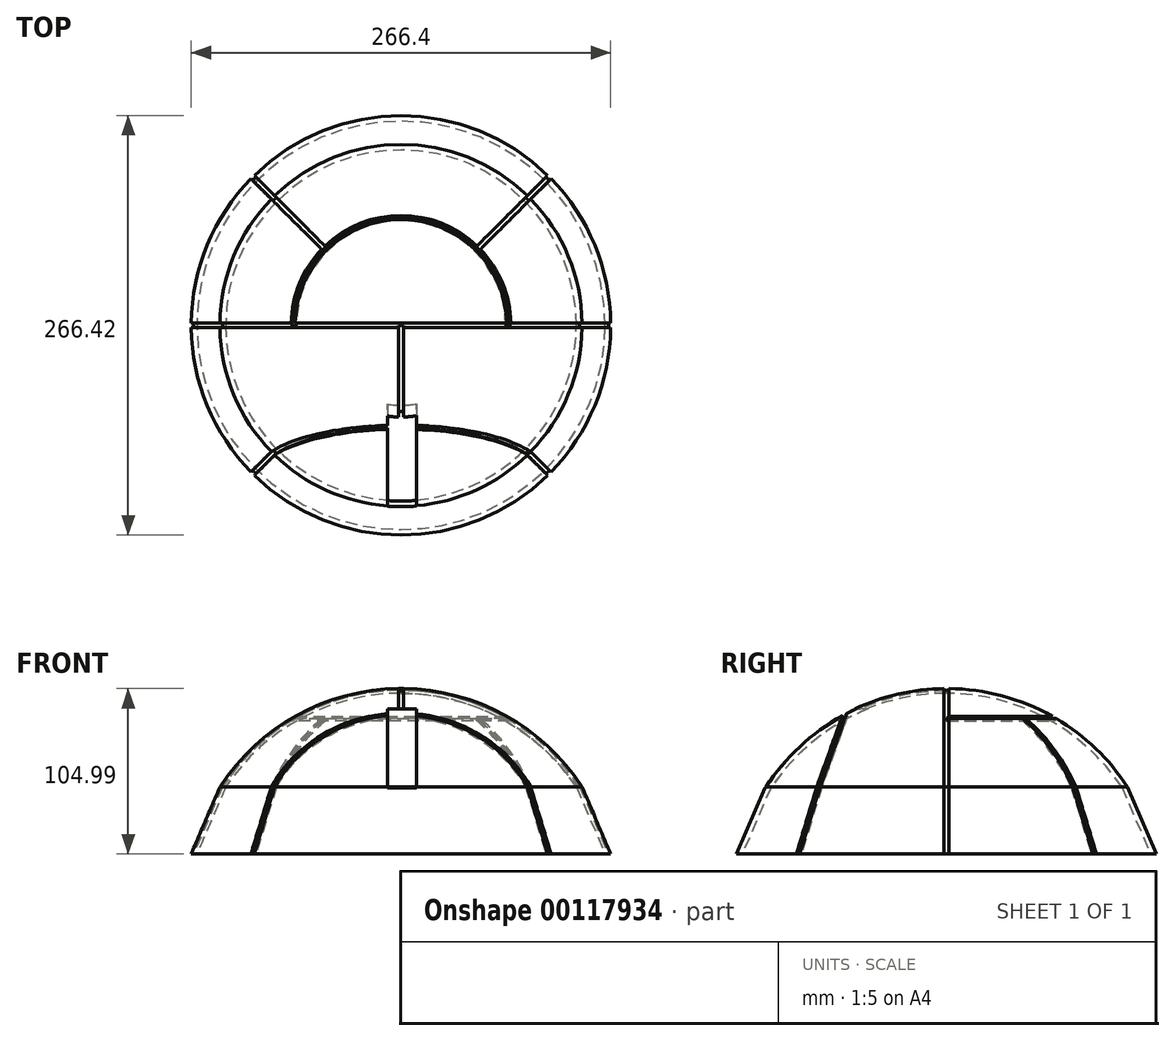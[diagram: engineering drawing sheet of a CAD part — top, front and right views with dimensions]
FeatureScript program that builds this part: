
annotation { "Feature Type Name" : "Feature", "Feature Type Description" : "" }
export const myFeature = defineFeature(function(context is Context, id is Id, definition is map)
    precondition{}
    {
        {
            var Q0;
            Q0=qCreatedBy(makeId("Front.planeOp"),FACE);
            var sketch = newSketch(context, id + "F0", { "sketchPlane" : qUnion([Q0])});
            skArc(sketch, "E0", {"start": v(114.97, 74.5) * mm, "mid": v(0, 137) * mm, "end": v(-114.97, 74.5) * mm});
            skLineSegment(sketch, "E1", {"start": v(-137, 0) * mm, "end": v(137, 0) * mm});
            skLineSegment(sketch, "E2", {"start": v(-133.21, 32) * mm, "end": v(133.21, 32) * mm});
            skLineSegment(sketch, "E3", {"start": v(-114.97, 74.5) * mm, "end": v(114.97, 74.5) * mm});
            skLineSegment(sketch, "E4", {"start": v(-114.97, 74.5) * mm, "end": v(-133.21, 32) * mm});
            skLineSegment(sketch, "E5", {"start": v(114.97, 74.5) * mm, "end": v(133.21, 32) * mm});
            skLineSegment(sketch, "E6", {"start": v(0, 137) * mm, "end": v(-99.44, 137) * mm, "construction": true});
            skLineSegment(sketch, "E7", {"start": v(0, 0) * mm, "end": v(0, 137) * mm});
            skArc(sketch, "E8", {"start": v(130.12, 32) * mm, "mid": v(0, 134) * mm, "end": v(-130.12, 32) * mm});
            skLineSegment(sketch, "E9", {"start": v(-111.38, 74.5) * mm, "end": v(-129.62, 32) * mm});
            skLineSegment(sketch, "E10", {"start": v(111.38, 74.5) * mm, "end": v(130.12, 32) * mm});
            skSolve(sketch);
        }
        {
            var Q0;
            {var subQ0=sQuery(id+"F0.wireOp",EDGE,"E4");Q0=makeQuery(id+"F0.imprint","IMPRINT",FACE,{"disambiguationData":[TD([[makeQuery(id+"F0.imprint","IMPRINT",EDGE,{"derivedFrom":subQ0}),1.0]])]});}
            var Q1;
            {var subQ0=sQuery(id+"F0.wireOp",EDGE,"E9");var subQ5=sQuery(id+"F0.wireOp",EDGE,"E2");var subQ7=makeQuery(id+"F0.imprint","INTERSECT",VERTEX,{"derivedFrom":[subQ5,subQ0]});Q1=makeQuery(id+"F0.imprint","IMPRINT",FACE,{"disambiguationData":[TD([[makeQuery(id+"F0.imprint","IMPRINT",EDGE,{"disambiguationData":[TD([[subQ7,1.0]])],"derivedFrom":subQ5}),1.0]])]});}
            var Q2;
            {var subQ0=sQuery(id+"F0.wireOp",EDGE,"y0KMc1JP-Vqzv-Jfck-pHGM-2HrRGkrfssAq");Q2=makeQuery(id+"F0.imprint","IMPRINT",FACE,{"disambiguationData":[TD([[makeQuery(id+"F0.imprint","IMPRINT",EDGE,{"derivedFrom":subQ0}),-1.0]])]});}
            var Q3;
            {var subQ1=sQuery(id+"F0.wireOp",EDGE,"E0");var subQ3=sQuery(id+"F0.wireOp",EDGE,"E7");var subQ4=makeQuery(id+"F0.imprint","INTERSECT",VERTEX,{"derivedFrom":[subQ1,subQ3]});Q3=makeQuery(id+"F0.imprint","IMPRINT",FACE,{"disambiguationData":[TD([[makeQuery(id+"F0.imprint","IMPRINT",EDGE,{"disambiguationData":[TD([[subQ4,1.0]])],"derivedFrom":subQ3}),1.0]])]});}
            var Q4;
            Q4=sQuery(id+"F0.wireOp",EDGE,"E7");
            revolve(context, id + "F1", {"entities" : qUnion([Q0, Q1, Q2, Q3]), "axis" : qUnion([Q4]), "revolveType" : RevolveType.FULL});
        }
        {
            var Q0;
            Q0=qCreatedBy(makeId("Top.planeOp"),FACE);
            cPlane(context, id + "F2", {"entities" : qUnion([Q0]), "cplaneType" : CPlaneType.OFFSET, "offset" : 74.5 * mm, "width" : 150 * mm, "height" : 150 * mm});
        }
        {
            var Q0;
            Q0=qCreatedBy(id+"F2.planeOp",FACE);
            var sketch = newSketch(context, id + "F3", { "sketchPlane" : qUnion([Q0])});
            skLineSegment(sketch, "E11", {"start": v(0, 0) * mm, "end": v(-58.68, 0) * mm, "construction": true});
            skLineSegment(sketch, "E12.bottom", {"start": v(-113.47, 1.5) * mm, "end": v(-116.47, 1.5) * mm});
            skLineSegment(sketch, "E12.top", {"start": v(-113.47, -1.5) * mm, "end": v(-116.47, -1.5) * mm});
            skLineSegment(sketch, "E12.left", {"start": v(-113.47, 1.5) * mm, "end": v(-113.47, -1.5) * mm});
            skLineSegment(sketch, "E12.right", {"start": v(-116.47, 1.5) * mm, "end": v(-116.47, -1.5) * mm});
            skPoint(sketch, "E12.middle", {"position": v(-114.97, 0) * mm});
            skLineSegment(sketch, "E13.1.0", {"start": v(-81.3, -79.18) * mm, "end": v(-83.42, -81.3) * mm});
            skLineSegment(sketch, "E13.1.1", {"start": v(-81.3, -79.18) * mm, "end": v(-79.18, -81.3) * mm});
            skLineSegment(sketch, "E13.1.2", {"start": v(-79.18, -81.3) * mm, "end": v(-81.3, -83.42) * mm});
            skLineSegment(sketch, "E13.1.3", {"start": v(-83.42, -81.3) * mm, "end": v(-81.3, -83.42) * mm});
            skLineSegment(sketch, "E13.2.0", {"start": v(-1.5, -113.47) * mm, "end": v(-1.5, -116.47) * mm});
            skLineSegment(sketch, "E13.2.1", {"start": v(-1.5, -113.47) * mm, "end": v(1.5, -113.47) * mm});
            skLineSegment(sketch, "E13.2.2", {"start": v(1.5, -113.47) * mm, "end": v(1.5, -116.47) * mm});
            skLineSegment(sketch, "E13.2.3", {"start": v(-1.5, -116.47) * mm, "end": v(1.5, -116.47) * mm});
            skLineSegment(sketch, "E13.3.0", {"start": v(79.18, -81.3) * mm, "end": v(81.3, -83.42) * mm});
            skLineSegment(sketch, "E13.3.1", {"start": v(79.18, -81.3) * mm, "end": v(81.3, -79.18) * mm});
            skLineSegment(sketch, "E13.3.2", {"start": v(81.3, -79.18) * mm, "end": v(83.42, -81.3) * mm});
            skLineSegment(sketch, "E13.3.3", {"start": v(81.3, -83.42) * mm, "end": v(83.42, -81.3) * mm});
            skLineSegment(sketch, "E13.4.0", {"start": v(113.47, -1.5) * mm, "end": v(116.47, -1.5) * mm});
            skLineSegment(sketch, "E13.4.1", {"start": v(113.47, -1.5) * mm, "end": v(113.47, 1.5) * mm});
            skLineSegment(sketch, "E13.4.2", {"start": v(113.47, 1.5) * mm, "end": v(116.47, 1.5) * mm});
            skLineSegment(sketch, "E13.4.3", {"start": v(116.47, -1.5) * mm, "end": v(116.47, 1.5) * mm});
            skLineSegment(sketch, "E13.5.0", {"start": v(81.3, 79.18) * mm, "end": v(83.42, 81.3) * mm});
            skLineSegment(sketch, "E13.5.1", {"start": v(81.3, 79.18) * mm, "end": v(79.18, 81.3) * mm});
            skLineSegment(sketch, "E13.5.2", {"start": v(79.18, 81.3) * mm, "end": v(81.3, 83.42) * mm});
            skLineSegment(sketch, "E13.5.3", {"start": v(83.42, 81.3) * mm, "end": v(81.3, 83.42) * mm});
            skLineSegment(sketch, "E13.6.0", {"start": v(1.5, 113.47) * mm, "end": v(1.5, 116.47) * mm});
            skLineSegment(sketch, "E13.6.1", {"start": v(1.5, 113.47) * mm, "end": v(-1.5, 113.47) * mm});
            skLineSegment(sketch, "E13.6.2", {"start": v(-1.5, 113.47) * mm, "end": v(-1.5, 116.47) * mm});
            skLineSegment(sketch, "E13.6.3", {"start": v(1.5, 116.47) * mm, "end": v(-1.5, 116.47) * mm});
            skLineSegment(sketch, "E13.7.0", {"start": v(-79.18, 81.3) * mm, "end": v(-81.3, 83.42) * mm});
            skLineSegment(sketch, "E13.7.1", {"start": v(-79.18, 81.3) * mm, "end": v(-81.3, 79.18) * mm});
            skLineSegment(sketch, "E13.7.2", {"start": v(-81.3, 79.18) * mm, "end": v(-83.42, 81.3) * mm});
            skLineSegment(sketch, "E13.7.3", {"start": v(-81.3, 83.42) * mm, "end": v(-83.42, 81.3) * mm});
            skPoint(sketch, "E13.center", {"position": v(0, 0) * mm});
            skLineSegment(sketch, "E14", {"start": v(81.3, -81.3) * mm, "end": v(-81.3, 81.3) * mm, "construction": true});
            skLineSegment(sketch, "E15", {"start": v(81.3, 81.3) * mm, "end": v(-81.3, -81.3) * mm, "construction": true});
            skLineSegment(sketch, "E16", {"start": v(-81.3, -81.3) * mm, "end": v(81.3, -81.3) * mm, "construction": true});
            skSolve(sketch);
        }
        {
            var Q0;
            Q0=makeQuery(id+"F3.imprint","IMPRINT",FACE,{"disambiguationData":[TD([[makeQuery(id+"F3.imprint","IMPRINT",EDGE,{"derivedFrom":sQuery(id+"F3.wireOp",EDGE,"E12.bottom")}),1.0]])]});
            var Q1;
            Q1=sQuery(id+"F0.wireOp",EDGE,"E4");
            sweep(context, id + "F4", {"operationType" : NewBodyOperationType.REMOVE, "profiles" : qUnion([Q0]), "path" : qUnion([Q1])});
        }
        {
            var Q0;
            Q0=makeQuery(id+"F3.imprint","IMPRINT",FACE,{"disambiguationData":[TD([[makeQuery(id+"F3.imprint","IMPRINT",EDGE,{"derivedFrom":sQuery(id+"F3.wireOp",EDGE,"E12.bottom")}),1.0]])]});
            var Q1;
            Q1=sQuery(id+"F0.wireOp",EDGE,"E0");
            sweep(context, id + "F5", {"operationType" : NewBodyOperationType.REMOVE, "profiles" : qUnion([Q0]), "path" : qUnion([Q1])});
        }
        {
            var Q0;
            Q0=makeQuery(id+"F3.imprint","IMPRINT",FACE,{"disambiguationData":[TD([[makeQuery(id+"F3.imprint","IMPRINT",EDGE,{"derivedFrom":sQuery(id+"F3.wireOp",EDGE,"E13.4.0")}),1.0]])]});
            var Q1;
            Q1=sQuery(id+"F0.wireOp",EDGE,"E5");
            sweep(context, id + "F6", {"operationType" : NewBodyOperationType.REMOVE, "profiles" : qUnion([Q0]), "path" : qUnion([Q1])});
        }
        {
            var Q0;
            Q0=qCreatedBy(makeId("Right.planeOp"),FACE);
            var sketch = newSketch(context, id + "F7", { "sketchPlane" : qUnion([Q0])});
            skArc(sketch, "E17", {"start": v(0, 137) * mm, "mid": v(-33.14, 132.93) * mm, "end": v(-64.32, 120.96) * mm});
            skLineSegment(sketch, "E18", {"start": v(0, 0) * mm, "end": v(-64.32, 120.96) * mm, "construction": true});
            skLineSegment(sketch, "E19", {"start": v(0, 137) * mm, "end": v(0, 0) * mm, "construction": true});
            skSolve(sketch);
        }
        {
            var Q0;
            Q0=qCreatedBy(makeId("Front.planeOp"),FACE);
            var sketch = newSketch(context, id + "F8", { "sketchPlane" : qUnion([Q0])});
            skLineSegment(sketch, "E20.bottom", {"start": v(1.5, 138.5) * mm, "end": v(-1.5, 138.5) * mm});
            skLineSegment(sketch, "E20.top", {"start": v(1.5, 135.5) * mm, "end": v(-1.5, 135.5) * mm});
            skLineSegment(sketch, "E20.left", {"start": v(1.5, 138.5) * mm, "end": v(1.5, 135.5) * mm});
            skLineSegment(sketch, "E20.right", {"start": v(-1.5, 138.5) * mm, "end": v(-1.5, 135.5) * mm});
            skPoint(sketch, "E20.middle", {"position": v(0, 137) * mm});
            skSolve(sketch);
        }
        {
            var Q0;
            Q0=makeQuery(id+"F8.imprint","IMPRINT",FACE,{"disambiguationData":[TD([[makeQuery(id+"F8.imprint","IMPRINT",EDGE,{"derivedFrom":sQuery(id+"F8.wireOp",EDGE,"E20.bottom")}),1.0]])]});
            var Q1;
            Q1=sQuery(id+"F7.wireOp",EDGE,"E17");
            sweep(context, id + "F9", {"operationType" : NewBodyOperationType.REMOVE, "profiles" : qUnion([Q0]), "path" : qUnion([Q1])});
        }
        {
            var Q0;
            Q0=qCreatedBy(makeId("Front.planeOp"),FACE);
            var sketch = newSketch(context, id + "F10", { "sketchPlane" : qUnion([Q0])});
            skCircle(sketch, "E21", {"center": v(0, 0) * mm, "radius": 137 * mm, "construction": true});
            skLineSegment(sketch, "E22", {"start": v(0, 0) * mm, "end": v(68.5, 118.65) * mm, "construction": true});
            skLineSegment(sketch, "E23", {"start": v(68.5, 118.65) * mm, "end": v(-68.5, 118.65) * mm});
            skLineSegment(sketch, "E24", {"start": v(-68.5, 118.65) * mm, "end": v(0, 0) * mm, "construction": true});
            skCircle(sketch, "E25", {"center": v(68.5, 118.65) * mm, "radius": 1.5 * mm});
            skLineSegment(sketch, "E26", {"start": v(67.75, 117.35) * mm, "end": v(69.05, 116.6) * mm});
            skLineSegment(sketch, "E27", {"start": v(69.05, 116.6) * mm, "end": v(70.55, 119.2) * mm});
            skLineSegment(sketch, "E28", {"start": v(67.75, 117.35) * mm, "end": v(66.45, 118.1) * mm});
            skLineSegment(sketch, "E29", {"start": v(70.55, 119.2) * mm, "end": v(67.95, 120.7) * mm});
            skLineSegment(sketch, "E30", {"start": v(67.95, 120.7) * mm, "end": v(66.45, 118.1) * mm});
            skSolve(sketch);
        }
        {
            var Q0;
            Q0=sQuery(id+"F10.wireOp",EDGE,"E23");
            cPlane(context, id + "F11", {"entities" : qUnion([Q0]), "cplaneType" : CPlaneType.LINE_ANGLE, "offset" : 25 * mm, "angle" : 90 * degree, "width" : 150 * mm, "height" : 150 * mm});
        }
        {
            var Q0;
            Q0=qCreatedBy(id+"F11.planeOp",FACE);
            var sketch = newSketch(context, id + "F12", { "sketchPlane" : qUnion([Q0])});
            skArc(sketch, "E31", {"start": v(68.5, 0) * mm, "mid": v(0, 68.5) * mm, "end": v(-68.5, 0) * mm});
            skLineSegment(sketch, "E32", {"start": v(-68.5, 0) * mm, "end": v(68.5, 0) * mm});
            skSolve(sketch);
        }
        {
            var Q0;
            {var subQ0=sQuery(id+"F10.wireOp",EDGE,"E25");var subQ3=makeQuery(id+"F10.imprint","INTERSECT",VERTEX,{"derivedFrom":[subQ0,sQuery(id+"F10.wireOp",EDGE,"E30")]});Q0=makeQuery(id+"F10.imprint","IMPRINT",FACE,{"disambiguationData":[TD([[makeQuery(id+"F10.imprint","IMPRINT",EDGE,{"disambiguationData":[TD([[subQ3,1.0]])],"derivedFrom":subQ0}),1.0]])]});}
            var Q1;
            {var subQ5=sQuery(id+"F10.wireOp",EDGE,"E28");Q1=makeQuery(id+"F10.imprint","IMPRINT",FACE,{"disambiguationData":[TD([[makeQuery(id+"F10.imprint","IMPRINT",EDGE,{"derivedFrom":subQ5}),-1.0]])]});}
            var Q2;
            {var subQ0=sQuery(id+"F10.wireOp",EDGE,"E30");var subQ1=sQuery(id+"F10.wireOp",EDGE,"E23");var subQ2=makeQuery(id+"F10.imprint","INTERSECT",VERTEX,{"derivedFrom":[subQ1,subQ0]});Q2=makeQuery(id+"F10.imprint","IMPRINT",FACE,{"disambiguationData":[TD([[makeQuery(id+"F10.imprint","IMPRINT",EDGE,{"disambiguationData":[TD([[subQ2,1.0]])],"derivedFrom":subQ1}),-1.0]])]});}
            var Q3;
            {var subQ0=sQuery(id+"F10.wireOp",EDGE,"E30");var subQ1=sQuery(id+"F10.wireOp",EDGE,"E25");var subQ2=makeQuery(id+"F10.imprint","INTERSECT",VERTEX,{"derivedFrom":[subQ1,subQ0]});Q3=makeQuery(id+"F10.imprint","IMPRINT",FACE,{"disambiguationData":[TD([[makeQuery(id+"F10.imprint","IMPRINT",EDGE,{"disambiguationData":[TD([[subQ2,1.0]])],"derivedFrom":subQ1}),-1.0]])]});}
            var Q4;
            {var subQ0=sQuery(id+"F10.wireOp",EDGE,"E29");var subQ1=sQuery(id+"F10.wireOp",EDGE,"E25");var subQ2=makeQuery(id+"F10.imprint","INTERSECT",VERTEX,{"derivedFrom":[subQ1,subQ0]});Q4=makeQuery(id+"F10.imprint","IMPRINT",FACE,{"disambiguationData":[TD([[makeQuery(id+"F10.imprint","IMPRINT",EDGE,{"disambiguationData":[TD([[subQ2,1.0]])],"derivedFrom":subQ1}),-1.0]])]});}
            var Q5;
            {var subQ0=sQuery(id+"F10.wireOp",EDGE,"E26");Q5=makeQuery(id+"F10.imprint","IMPRINT",FACE,{"disambiguationData":[TD([[makeQuery(id+"F10.imprint","IMPRINT",EDGE,{"derivedFrom":subQ0}),1.0]])]});}
            var Q6;
            Q6=sQuery(id+"F12.wireOp",EDGE,"E31");
            sweep(context, id + "F13", {"operationType" : NewBodyOperationType.REMOVE, "profiles" : qUnion([Q0, Q1, Q2, Q3, Q4, Q5]), "path" : qUnion([Q6])});
        }
        {
            var Q0;
            Q0=sQuery(id+"F3.wireOp",EDGE,"E15");
            cPlane(context, id + "F14", {"entities" : qUnion([Q0]), "cplaneType" : CPlaneType.LINE_ANGLE, "offset" : 25 * mm, "angle" : 90 * degree, "width" : 150 * mm, "height" : 150 * mm});
        }
        {
            var Q0;
            Q0=qCreatedBy(id+"F14.planeOp",FACE);
            var sketch = newSketch(context, id + "F15", { "sketchPlane" : qUnion([Q0])});
            skLineSegment(sketch, "E33", {"start": v(202.35, 74.5) * mm, "end": v(-236.58, 74.5) * mm, "construction": true});
            skLineSegment(sketch, "E34", {"start": v(177.5, 32) * mm, "end": v(-236.58, 32) * mm, "construction": true});
            skLineSegment(sketch, "E35", {"start": v(114.93, 74.5) * mm, "end": v(133.21, 32) * mm});
            skLineSegment(sketch, "E36", {"start": v(69.47, 117.89) * mm, "end": v(69.47, 32) * mm});
            skLineSegment(sketch, "E37", {"start": v(69.47, 32) * mm, "end": v(133.21, 32) * mm});
            skArc(sketch, "E38.trimOffspring", {"start": v(115.04, 74.26) * mm, "mid": v(94.8, 98.73) * mm, "end": v(69.47, 117.89) * mm});
            skSolve(sketch);
        }
        {
            var Q0;
            Q0=makeQuery(id+"F3.imprint","IMPRINT",FACE,{"disambiguationData":[TD([[makeQuery(id+"F3.imprint","IMPRINT",EDGE,{"derivedFrom":sQuery(id+"F3.wireOp",EDGE,"E13.5.0")}),1.0]])]});
            var Q1;
            Q1=sQuery(id+"F15.wireOp",EDGE,"E35");
            sweep(context, id + "F16", {"operationType" : NewBodyOperationType.REMOVE, "profiles" : qUnion([Q0]), "path" : qUnion([Q1])});
        }
        {
            var Q0;
            Q0=makeQuery(id+"F3.imprint","IMPRINT",FACE,{"disambiguationData":[TD([[makeQuery(id+"F3.imprint","IMPRINT",EDGE,{"derivedFrom":sQuery(id+"F3.wireOp",EDGE,"E13.5.0")}),1.0]])]});
            var Q1;
            Q1=sQuery(id+"F15.wireOp",EDGE,"E38.trimOffspring");
            sweep(context, id + "F17", {"operationType" : NewBodyOperationType.REMOVE, "profiles" : qUnion([Q0]), "path" : qUnion([Q1])});
        }
        {
            var Q0;
            Q0=sQuery(id+"F3.wireOp",EDGE,"E14");
            cPlane(context, id + "F18", {"entities" : qUnion([Q0]), "cplaneType" : CPlaneType.LINE_ANGLE, "offset" : 25 * mm, "angle" : 90 * degree, "width" : 150 * mm, "height" : 150 * mm});
        }
        {
            var Q0;
            Q0=qCreatedBy(id+"F18.planeOp",FACE);
            var sketch = newSketch(context, id + "F19", { "sketchPlane" : qUnion([Q0])});
            skArc(sketch, "E39", {"start": v(-114.97, 74.5) * mm, "mid": v(-125.9, 54.03) * mm, "end": v(-133.21, 32) * mm});
            skLineSegment(sketch, "E40", {"start": v(-154.96, 32) * mm, "end": v(196.04, 32) * mm, "construction": true});
            skLineSegment(sketch, "E41", {"start": v(-136.76, 74.5) * mm, "end": v(202.22, 74.5) * mm, "construction": true});
            skLineSegment(sketch, "E42", {"start": v(114.97, 74.5) * mm, "end": v(133.21, 32) * mm});
            skLineSegment(sketch, "E43", {"start": v(68.48, 118.66) * mm, "end": v(68.48, 32) * mm});
            skLineSegment(sketch, "E44", {"start": v(68.48, 32) * mm, "end": v(133.21, 32) * mm});
            skArc(sketch, "E45.trimOffspring", {"start": v(114.97, 74.5) * mm, "mid": v(94.35, 99.34) * mm, "end": v(68.48, 118.66) * mm});
            skSolve(sketch);
        }
        {
            var Q0;
            Q0=makeQuery(id+"F3.imprint","IMPRINT",FACE,{"disambiguationData":[TD([[makeQuery(id+"F3.imprint","IMPRINT",EDGE,{"derivedFrom":sQuery(id+"F3.wireOp",EDGE,"E13.7.0")}),1.0]])]});
            var Q1;
            Q1=sQuery(id+"F19.wireOp",EDGE,"E42");
            sweep(context, id + "F20", {"operationType" : NewBodyOperationType.REMOVE, "profiles" : qUnion([Q0]), "path" : qUnion([Q1])});
        }
        {
            var Q0;
            Q0=makeQuery(id+"F3.imprint","IMPRINT",FACE,{"disambiguationData":[TD([[makeQuery(id+"F3.imprint","IMPRINT",EDGE,{"derivedFrom":sQuery(id+"F3.wireOp",EDGE,"E13.7.0")}),1.0]])]});
            var Q1;
            Q1=sQuery(id+"F19.wireOp",EDGE,"E45.trimOffspring");
            sweep(context, id + "F21", {"operationType" : NewBodyOperationType.REMOVE, "profiles" : qUnion([Q0]), "path" : qUnion([Q1])});
        }
        {
            var Q0;
            Q0=sQuery(id+"F15.wireOp",EDGE,"E34");
            cPlane(context, id + "F22", {"entities" : qUnion([Q0]), "cplaneType" : CPlaneType.LINE_ANGLE, "offset" : 25 * mm, "angle" : 90 * degree, "width" : 150 * mm, "height" : 150 * mm});
        }
        {
            var Q0;
            Q0=qCreatedBy(id+"F22.planeOp",FACE);
            var sketch = newSketch(context, id + "F23", { "sketchPlane" : qUnion([Q0])});
            skArc(sketch, "E46", {"start": v(-133.21, 32) * mm, "mid": v(125.9, -54.03) * mm, "end": v(-114.97, 74.5) * mm});
            skLineSegment(sketch, "E47", {"start": v(-186.25, 32) * mm, "end": v(184.2, 32) * mm, "construction": true});
            skLineSegment(sketch, "E48", {"start": v(-158.48, 74.5) * mm, "end": v(175.2, 74.5) * mm, "construction": true});
            skLineSegment(sketch, "E49", {"start": v(-114.97, 74.5) * mm, "end": v(-133.21, 32) * mm});
            skSolve(sketch);
        }
        {
            var Q0;
            Q0=makeQuery(id+"F3.imprint","IMPRINT",FACE,{"disambiguationData":[TD([[makeQuery(id+"F3.imprint","IMPRINT",EDGE,{"derivedFrom":sQuery(id+"F3.wireOp",EDGE,"E13.1.0")}),1.0]])]});
            var Q1;
            Q1=sQuery(id+"F23.wireOp",EDGE,"E49");
            sweep(context, id + "F24", {"operationType" : NewBodyOperationType.REMOVE, "profiles" : qUnion([Q0]), "path" : qUnion([Q1])});
        }
        {
            var Q0;
            Q0=sQuery(id+"F19.wireOp",EDGE,"E40");
            cPlane(context, id + "F25", {"entities" : qUnion([Q0]), "cplaneType" : CPlaneType.LINE_ANGLE, "offset" : 25 * mm, "angle" : 90 * degree, "width" : 150 * mm, "height" : 150 * mm});
        }
        {
            var Q0;
            Q0=qCreatedBy(id+"F25.planeOp",FACE);
            var sketch = newSketch(context, id + "F26", { "sketchPlane" : qUnion([Q0])});
            skArc(sketch, "E50", {"start": v(-133.21, 32) * mm, "mid": v(125.9, -54.03) * mm, "end": v(-114.97, 74.5) * mm});
            skLineSegment(sketch, "E51", {"start": v(-151.8, 74.5) * mm, "end": v(39.62, 74.5) * mm, "construction": true});
            skLineSegment(sketch, "E52", {"start": v(-155.93, 32) * mm, "end": v(41.16, 32) * mm, "construction": true});
            skLineSegment(sketch, "E53", {"start": v(-114.97, 74.5) * mm, "end": v(-133.21, 32) * mm});
            skSolve(sketch);
        }
        {
            var Q0;
            Q0=makeQuery(id+"F3.imprint","IMPRINT",FACE,{"disambiguationData":[TD([[makeQuery(id+"F3.imprint","IMPRINT",EDGE,{"derivedFrom":sQuery(id+"F3.wireOp",EDGE,"E13.3.0")}),1.0]])]});
            var Q1;
            Q1=sQuery(id+"F26.wireOp",EDGE,"E53");
            sweep(context, id + "F27", {"operationType" : NewBodyOperationType.REMOVE, "profiles" : qUnion([Q0]), "path" : qUnion([Q1])});
        }
        {
            var Q0;
            Q0=sQuery(id+"F3.wireOp",EDGE,"E16");
            cPlane(context, id + "F28", {"entities" : qUnion([Q0]), "cplaneType" : CPlaneType.LINE_ANGLE, "offset" : 25 * mm, "angle" : 340 * degree, "width" : 150 * mm, "height" : 150 * mm});
        }
        {
            var Q0;
            Q0=qCreatedBy(id+"F28.planeOp",FACE);
            var sketch = newSketch(context, id + "F29", { "sketchPlane" : qUnion([Q0])});
            skArc(sketch, "E54", {"start": v(81.3, 42.2) * mm, "mid": v(0, 91.25) * mm, "end": v(-81.3, 42.2) * mm});
            skSolve(sketch);
        }
        {
            var Q0;
            Q0=makeQuery(id+"F3.imprint","IMPRINT",FACE,{"disambiguationData":[TD([[makeQuery(id+"F3.imprint","IMPRINT",EDGE,{"derivedFrom":sQuery(id+"F3.wireOp",EDGE,"E13.1.0")}),1.0]])]});
            var Q1;
            Q1=sQuery(id+"F29.wireOp",EDGE,"E54");
            sweep(context, id + "F30", {"operationType" : NewBodyOperationType.REMOVE, "profiles" : qUnion([Q0]), "path" : qUnion([Q1])});
        }
        {
            var Q0;
            Q0=qCreatedBy(makeId("Front.planeOp"),FACE);
            cPlane(context, id + "F31", {"entities" : qUnion([Q0]), "cplaneType" : CPlaneType.OFFSET, "offset" : 150 * mm, "width" : 150 * mm, "height" : 150 * mm});
        }
        {
            var Q0;
            Q0=qCreatedBy(id+"F31.planeOp",FACE);
            var sketch = newSketch(context, id + "F32", { "sketchPlane" : qUnion([Q0])});
            skLineSegment(sketch, "E55", {"start": v(0, 0) * mm, "end": v(0, 142.08) * mm, "construction": true});
            skLineSegment(sketch, "E56.bottom", {"start": v(-8.62, 124) * mm, "end": v(10, 124) * mm});
            skLineSegment(sketch, "E56.top", {"start": v(-8.62, 74) * mm, "end": v(10, 74) * mm});
            skLineSegment(sketch, "E56.left", {"start": v(-8.62, 124) * mm, "end": v(-8.62, 74) * mm});
            skLineSegment(sketch, "E56.right", {"start": v(10, 124) * mm, "end": v(10, 74) * mm});
            skSolve(sketch);
        }
        {
            var Q0;
            Q0=makeQuery(id+"F32.imprint","IMPRINT",FACE,{"disambiguationData":[TD([[makeQuery(id+"F32.imprint","IMPRINT",EDGE,{"derivedFrom":sQuery(id+"F32.wireOp",EDGE,"E56.bottom")}),-1.0]])]});
            extrude(context, id + "F33", {"entities" : qUnion([Q0]), "operationType" : NewBodyOperationType.REMOVE, "oppositeDirection" : true, "depth" : 123.02 * mm});
        }
    });
